# Revit family: Sanitary_Shower-screens_Duscholux_D1ModeOne_Slider-twin-doors-shower
name_source: partatom
category: Aparatos sanitarios
units: mm (PartAtom-declared; Revit-internal decimal feet)

## family parameters
Compartido = No
Corte con vacíos al cargar = No
Cota de conector redondo = Diámetro de uso
Número OmniClass = 23.45.00.00
Punto de cálculo de habitación = No
Se basa en plano de trabajo = No
Siempre vertical = Sí
Tipo de pieza = Normal
Título OmniClass = Sanitary, Laundry, and Cleaning Equipment

## types (2) — shared parameters
Anti-Lime Treatment = FeelNet 3D Included
Brand = Duscholux
Certified Quality UNE EN 14428 = http://www.duscholux.es
Components = Eropean components
Configuration enclosure = https://configuratumampara.duscholux.es
Código de montaje = C1030200
Descripción = 2 fixed segments + slider twin doors
Design country = Germany
Edition number = 1
Environmental Management ISO 14001 = ECOEMBES Certificate
Fabricante = Duscholux Ibérica, S.A.
Fact sheet = https://www.duscholux.es
Glass Material = Glass_Material-Duscholux
Glass in Building UNE EN 12150 = CE Conformity marking
Handle Height = 1000 mm  [stored 3.28084 ft]
Height = 2000 mm  [stored 6.56168 ft]
IFC Classification = Furnishing Element
Image = https://www.duscholux.es
Maintenance and Cleaning = http://www.duscholux.es
Manufacturer country = Spain / Germany
Manufacturer name = Duscholux Ibérica, S.A.
Max Height = 2000 mm  [stored 6.56168 ft]
Min Max Width = 1500 mm  [stored 4.92126 ft]
NBS Reference Code = 45-35-70
NBS Reference Description = Shower Enclosures
Net Weight (Kg) = 63
Opening System = Sliding
Opening System Image = http://blob.duscholux.es
Product family = D1 Mode One
Product group = Front for shower
Products = http://www.duscholux.es
Ref. = KMB
Sliding Door Width = 381 mm
Technical Inspection Certificate (Applus) = http://www.duscholux.es
Thickness Safety Glass Fixed Panel = 6 mm  [stored 0.019685 ft]
Thickness Safety Glass Sliding = 6 mm  [stored 0.019685 ft]
UNSPSC Code = 30181507
URL = http://www.duscholux.es
Uniclass 2015 Code = PR-40-20-06-79
Uniclass 2015 Description = Shower Enclosures
Width = 1500 mm  [stored 4.92126 ft]
zero-valued in all types: Opening Door, Opening Percentage

## per-type parameters (varying)
| type | Accesories Material | Frame Material | Handle Material | Series |
| Platinum Aluminium Finish | Chrome_Finish | Platinum Aluminium Finish | Chrome_Finish | D1 Mode One |
| Black Aluminium Finish | Anodized Aluminium_Duscholux Material-Black Finish | Anodized Aluminium_Duscholux Material-Black Finish | Anodized Aluminium_Duscholux Material-Black Finish | D1 Mode One24 |

note: [stored X ft] marks values corroborated as IEEE doubles in the binary element streams (Revit-internal decimal feet)
